# Revit family: 207_c2f4fe7933144737ab2d66dfcad04a
name_source: partatom
category: Air Terminals
revit_build: Autodesk Revit 2018 (Build: 20170223_1515(x64)
units: mm (PartAtom-declared; Revit-internal decimal feet)

## family parameters
Always vertical = Yes
Cut with Voids When Loaded = No
Part Type = Normal
Room Calculation Point = Yes
Round Connector Dimension = Use Diameter
Shared = No
Work Plane-Based = No

## types (1)
- 200-116528
    A2 = 200 mm  [stored 0.656168 ft]
    B1 = 400 mm  [stored 1.31234 ft]
    B12 = 200 mm  [stored 0.656168 ft]
    CAT0 = Yes
    CLBTZ = 0 mm  [stored 0 ft]
    CL_Location_5000 = 5000 mm  [stored 16.4042 ft]
    D = 200 mm
    Description = Roof hood flat roof black
    H_ARR = 0 mm  [stored 0 ft]
    L2 = 500 mm  [stored 1.64042 ft]
    L22 = 250 mm  [stored 0.82021 ft]
    L_ARR = 400 mm  [stored 1.31234 ft]
    MC Product Code = 200-116528
    Manufacturer = Flexit
    QmdConnectorList = 201;D
    URL = www.flexit.no
    W_ARR = 400 mm  [stored 1.31234 ft]
    Z = 25 mm  [stored 0.082021 ft]
    Z2 = 25 mm  [stored 0.082021 ft]
    magiPartTypeId = 207
    magiProductFamilyId = c2f4fe7933144737ab2d66dfcad04a
    magiProductId = 91de5f68029345598f329e17747752

note: [stored X ft] marks values corroborated as IEEE doubles in the binary element streams (Revit-internal decimal feet)

## geometry (parser evidence)
native form markers: Sweep x2
no freeform markers — native parametric forms only
